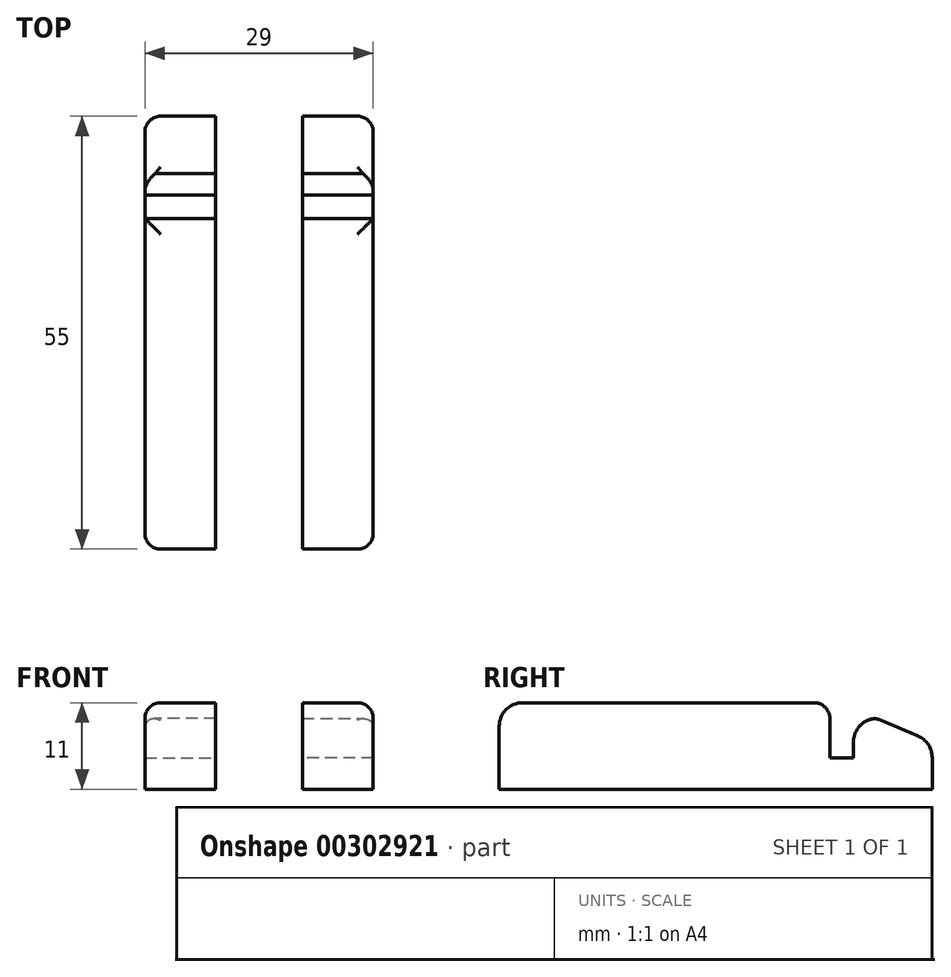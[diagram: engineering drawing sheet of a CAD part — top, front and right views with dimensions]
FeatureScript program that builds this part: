
annotation { "Feature Type Name" : "Feature", "Feature Type Description" : "" }
export const myFeature = defineFeature(function(context is Context, id is Id, definition is map)
    precondition{}
    {
        {
            var Q0;
            Q0=qCreatedBy(makeId("Top.planeOp"),FACE);
            var sketch = newSketch(context, id + "F0", { "sketchPlane" : qUnion([Q0])});
            skLineSegment(sketch, "E0.bottom", {"start": v(4.5, 27.5) * mm, "end": v(-4.5, 27.5) * mm});
            skLineSegment(sketch, "E0.top", {"start": v(4.5, -27.5) * mm, "end": v(-4.5, -27.5) * mm});
            skLineSegment(sketch, "E0.left", {"start": v(4.5, 27.5) * mm, "end": v(4.5, -27.5) * mm});
            skLineSegment(sketch, "E0.right", {"start": v(-4.5, 27.5) * mm, "end": v(-4.5, -27.5) * mm});
            skPoint(sketch, "E0.middle", {"position": v(0, 0) * mm});
            skLineSegment(sketch, "E1", {"start": v(-4.5, 17.5) * mm, "end": v(4.5, 17.5) * mm});
            skLineSegment(sketch, "E2", {"start": v(-4.5, 14.5) * mm, "end": v(4.5, 14.5) * mm});
            skSolve(sketch);
        }
        {
            var Q0;
            {var subQ0=sQuery(id+"F0.wireOp",EDGE,"E1");Q0=makeQuery(id+"F0.imprint","IMPRINT",FACE,{"disambiguationData":[TD([[makeQuery(id+"F0.imprint","IMPRINT",EDGE,{"derivedFrom":subQ0}),-1.0]])]});}
            extrude(context, id + "F1", {"entities" : qUnion([Q0]), "depth" : 4 * mm});
        }
        {
            var Q0;
            {var subQ0=sQuery(id+"F0.wireOp",EDGE,"E0.bottom");Q0=makeQuery(id+"F0.imprint","IMPRINT",FACE,{"disambiguationData":[TD([[makeQuery(id+"F0.imprint","IMPRINT",EDGE,{"derivedFrom":subQ0}),1.0]])]});}
            extrude(context, id + "F2", {"entities" : qUnion([Q0]), "operationType" : NewBodyOperationType.ADD, "depth" : 9 * mm});
        }
        {
            var Q0;
            {var subQ0=sQuery(id+"F0.wireOp",EDGE,"E0.top");Q0=makeQuery(id+"F0.imprint","IMPRINT",FACE,{"disambiguationData":[TD([[makeQuery(id+"F0.imprint","IMPRINT",EDGE,{"derivedFrom":subQ0}),-1.0]])]});}
            extrude(context, id + "F3", {"entities" : qUnion([Q0]), "operationType" : NewBodyOperationType.ADD, "depth" : 11 * mm});
        }
        {
            var Q0;
            Q0=makeQuery(id+"F2.opExtrude","CAP_EDGE",EDGE,{"disambiguationData":[OSD([sQuery(id+"F0.wireOp",EDGE,"E0.bottom")])],"isStart":false});
            chamfer(context, id + "F4", {"entities" : qUnion([Q0]), "chamferType" : ChamferType.TWO_OFFSETS, "width1" : 7 * mm, "oppositeDirection" : false, "width2" : 3 * mm, "tangentPropagation" : true});
        }
        {
            var Q0;
            Q0=makeQuery(id+"F2.opExtrude","CAP_EDGE",EDGE,{"disambiguationData":[OSD([sQuery(id+"F0.wireOp",EDGE,"E1")])],"isStart":false});
            var Q1;
            {var subQ0=sQuery(id+"F0.wireOp",EDGE,"E0.bottom");Q1=makeQuery(id+"F4.opChamfer","BLEND_EDGE",EDGE,{"blendedFrom":[makeQuery(id+"F2.opExtrude","CAP_EDGE",EDGE,{"disambiguationData":[OSD([subQ0])],"isStart":false}),makeQuery(id+"F2.opExtrude","SWEPT_FACE",FACE,{"disambiguationData":[OSD([subQ0])]})],"blendedInto":[makeQuery(id+"F2.opExtrude","SWEPT_FACE",FACE,{"disambiguationData":[OSD([subQ0])]})]});}
            var Q2;
            {var subQ0=sQuery(id+"F0.wireOp",EDGE,"E0.bottom");Q2=makeQuery(id+"F4.opChamfer","BLEND_EDGE",EDGE,{"blendedFrom":[makeQuery(id+"F2.opExtrude","CAP_EDGE",EDGE,{"disambiguationData":[OSD([subQ0])],"isStart":false}),makeQuery(id+"F2.opExtrude","CAP_FACE",FACE,{"disambiguationData":[OSD([subQ0,sQuery(id+"F0.wireOp",EDGE,"E0.left"),sQuery(id+"F0.wireOp",EDGE,"E0.right"),sQuery(id+"F0.wireOp",EDGE,"E1")])],"isStart":false})],"blendedInto":[makeQuery(id+"F2.opExtrude","CAP_FACE",FACE,{"disambiguationData":[OSD([subQ0,sQuery(id+"F0.wireOp",EDGE,"E0.left"),sQuery(id+"F0.wireOp",EDGE,"E0.right"),sQuery(id+"F0.wireOp",EDGE,"E1")])],"isStart":false})]});}
            var Q3;
            Q3=makeQuery(id+"F3.opExtrude","CAP_EDGE",EDGE,{"disambiguationData":[OSD([sQuery(id+"F0.wireOp",EDGE,"E0.top")])],"isStart":false});
            fillet(context, id + "F5", {"entities" : qUnion([Q0, Q1, Q2, Q3]), "radius" : 3 * mm, "tangentPropagation" : true, "allowEdgeOverflow" : false});
        }
        {
            var Q0;
            Q0=makeQuery(id+"F3.opExtrude","CAP_EDGE",EDGE,{"disambiguationData":[OSD([sQuery(id+"F0.wireOp",EDGE,"E2")])],"isStart":false});
            var Q1;
            Q1=makeQuery(id+"F3.opExtrude","CAP_EDGE",EDGE,{"disambiguationData":[OSD([sQuery(id+"F0.wireOp",EDGE,"E0.right")])],"isStart":false});
            var Q2;
            {var subQ0=sQuery(id+"F0.wireOp",EDGE,"E0.right");Q2=makeQuery(id+"F4.opChamfer","BLEND_EDGE",EDGE,{"blendedFrom":[makeQuery(id+"F2.opExtrude","CAP_EDGE",EDGE,{"disambiguationData":[OSD([sQuery(id+"F0.wireOp",EDGE,"E0.bottom")])],"isStart":false}),makeQuery(id+"F3.boolean.opBoolean","MERGE",FACE,{"derivedFrom":[makeQuery(id+"F2.boolean.opBoolean","MERGE",FACE,{"derivedFrom":[makeQuery(id+"F1.opExtrude","SWEPT_FACE",FACE,{"disambiguationData":[OSD([subQ0])]}),makeQuery(id+"F2.opExtrude","SWEPT_FACE",FACE,{"disambiguationData":[OSD([subQ0])]})]}),makeQuery(id+"F3.opExtrude","SWEPT_FACE",FACE,{"disambiguationData":[OSD([subQ0])]})]})],"blendedInto":[makeQuery(id+"F3.boolean.opBoolean","MERGE",FACE,{"derivedFrom":[makeQuery(id+"F2.boolean.opBoolean","MERGE",FACE,{"derivedFrom":[makeQuery(id+"F1.opExtrude","SWEPT_FACE",FACE,{"disambiguationData":[OSD([subQ0])]}),makeQuery(id+"F2.opExtrude","SWEPT_FACE",FACE,{"disambiguationData":[OSD([subQ0])]})]}),makeQuery(id+"F3.opExtrude","SWEPT_FACE",FACE,{"disambiguationData":[OSD([subQ0])]})]})]});}
            fillet(context, id + "F6", {"entities" : qUnion([Q0, Q1, Q2]), "radius" : 2 * mm, "tangentPropagation" : true, "allowEdgeOverflow" : false});
        }
        {
            var Q0;
            Q0=qCreatedBy(makeId("Right.planeOp"),FACE);
            cPlane(context, id + "F7", {"entities" : qUnion([Q0]), "cplaneType" : CPlaneType.OFFSET, "offset" : 10 * mm, "width" : 150 * mm, "height" : 150 * mm});
        }
        {
            var Q0;
            Q0=makeQuery(id+"F1.opExtrude","SWEPT_BODY",BODY,{"disambiguationData":[OSD([sQuery(id+"F0.wireOp",EDGE,"E0.left"),sQuery(id+"F0.wireOp",EDGE,"E0.right"),sQuery(id+"F0.wireOp",EDGE,"E1"),sQuery(id+"F0.wireOp",EDGE,"E2")])]});
            var Q1;
            Q1=qCreatedBy(id+"F7.planeOp",FACE);
            mirror(context, id + "F8", {"entities" : qUnion([Q0]), "mirrorPlane" : qUnion([Q1])});
        }
    });
